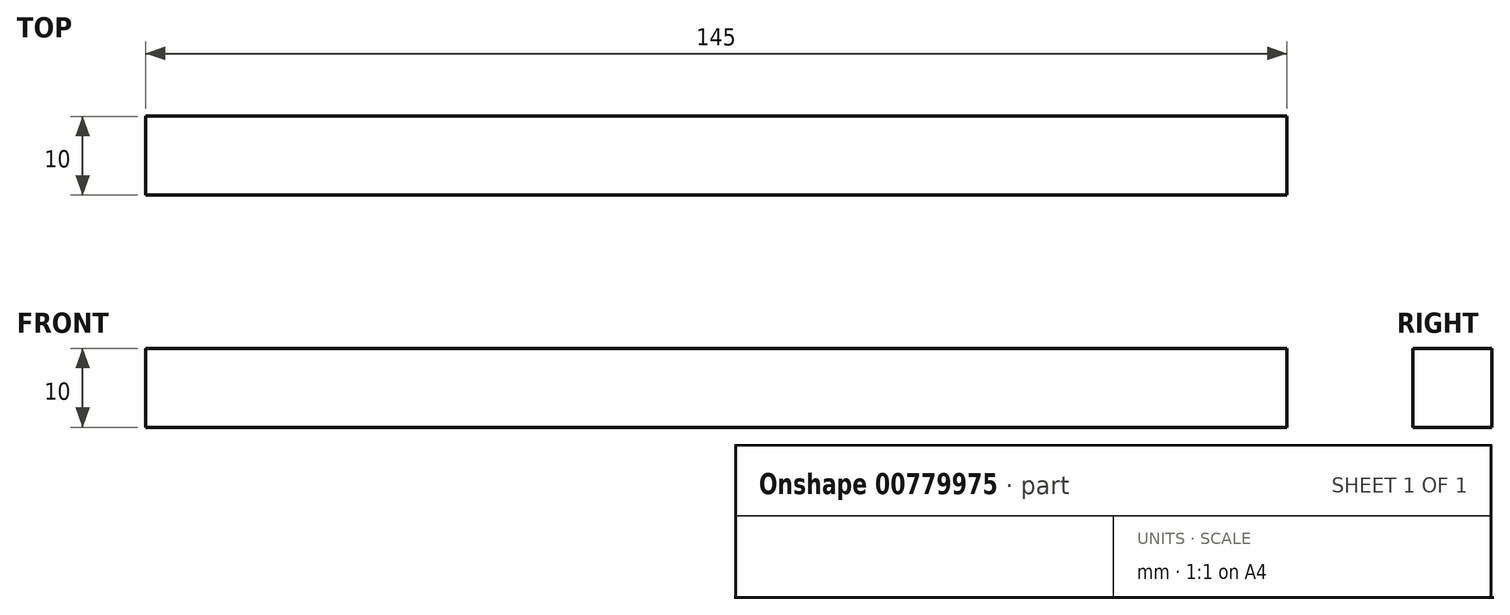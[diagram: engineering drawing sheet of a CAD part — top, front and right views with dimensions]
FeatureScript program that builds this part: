
annotation { "Feature Type Name" : "Feature", "Feature Type Description" : "" }
export const myFeature = defineFeature(function(context is Context, id is Id, definition is map)
    precondition{}
    {
        {
            var Q0;
            Q0=qCreatedBy(makeId("Top.planeOp"),FACE);
            var sketch = newSketch(context, id + "F0", { "sketchPlane" : qUnion([Q0])});
            skLineSegment(sketch, "E0", {"start": v(-52.8, 20.62) * mm, "end": v(92.2, 20.62) * mm});
            skLineSegment(sketch, "E1", {"start": v(92.2, 20.62) * mm, "end": v(92.2, 10.62) * mm});
            skLineSegment(sketch, "E2", {"start": v(92.2, 10.62) * mm, "end": v(-52.8, 10.62) * mm});
            skLineSegment(sketch, "E3", {"start": v(-52.8, 10.62) * mm, "end": v(-52.8, 20.62) * mm});
            skSolve(sketch);
        }
        {
            var Q0;
            Q0 = qSketchRegion(id + "F0", true);
            extrude(context, id + "F1", {"entities" : qUnion([Q0]), "depth" : 10 * mm, "offsetDistance" : 25 * mm});
        }
    });
